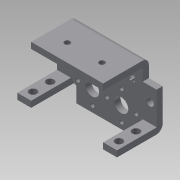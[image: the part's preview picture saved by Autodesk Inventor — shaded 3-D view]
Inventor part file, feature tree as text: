
AUTODESK INVENTOR PART (.ipt)
format: ipt  version: 2015 SP1 (Build 190203100, 203)  size: 531,456 bytes
history: native  units: mm
features: sketch x19, extrude x18, reference x11, projected_geometry x7, fillet x3, mirror x3
ambient origin geometry x8: Origin, YZ Plane, XZ Plane, XY Plane, X Axis, Y Axis, Z Axis, Center Point
bodies: Solid1 (feature_tree)
feature tree (61):
  extrude  "Extrusion1"  Depth=29.21mm
  extrude  "Extrusion2"  Depth=3.5mm
  extrude  "Extrusion3"  Depth=57.15mm TaperAngle=0.0deg
  sketch  "Sketch5"  dims[d8=57.15mm d9=0.0mm d11=25.147mm d12=0.0mm d13=0.254mm]
  extrude  "Extrusion4"  Depth=0.254mm TaperAngle=0.0deg
  fillet  "Fillet1"  Radius=0.254mm
  extrude  "Extrusion5"  Depth=3.75mm
  mirror  "Mirror1"
  fillet  "Fillet2"  Radius=22.4282mm
  extrude  "Extrusion6"  Depth=25.147mm TaperAngle=0.0deg
  extrude  "Extrusion7"  Depth=3.5mm TaperAngle=0.0deg
  extrude  "Extrusion8"  Depth=3.5mm TaperAngle=0.0deg
  extrude  "Extrusion9"  Depth=22.682mm TaperAngle=0.0deg
  extrude  "Extrusion10"  Depth=7.95mm TaperAngle=0.0deg
  sketch  "Sketch16"  dims[d38=7.95mm d39=0.0mm d43=7.95mm d44=0.0mm d47=3.5mm d48=0.0mm]
  extrude  "Extrusion11"  Depth=7.95mm TaperAngle=0.0deg
  fillet  "Fillet3"  Radius=3.5mm
  sketch  "Sketch19"  dims[d50=2.0mm d51=3.5mm d52=0.0mm]
  extrude  "Extrusion12"  Depth=3.5mm TaperAngle=0.0deg
  mirror  "Mirror2"
  extrude  "Extrusion13"  Depth=3.5mm TaperAngle=0.0deg
  extrude  "Extrusion15"  [1 undecoded]
  sketch  "Sketch24"
  sketch  "Sketch25"
  extrude  "Extrusion17"  [1 undecoded]
  extrude  "Extrusion18"  [1 undecoded]
  mirror  "Mirror4"
  extrude  "Extrusion19"  [1 undecoded]
  extrude  "Extrusion20"  [1 undecoded]
  sketch  "Sketch1"  dims[d0=57.15mm d1=29.21mm]
  sketch  "Sketch2"  dims[d2=3.5mm d3=0.0mm d4=3.5mm]
  sketch  "Sketch4"  dims[d5=3.5mm d6=57.15mm d7=0.0mm]
  sketch  "Sketch9"  dims[d15=25.147mm d16=0.0mm d17=3.75mm d18=22.4282mm]
  reference  "Reference3"
  reference  "Reference4"
  sketch  "Sketch11"  dims[d19=22.428mm d20=25.147mm d21=0.0mm]
  reference  "Reference7"
  sketch  "Sketch12"  dims[d22=25.147mm d23=0.0mm d24=3.5mm d25=0.0mm]
  reference  "Reference8"
  reference  "Reference9"
  sketch  "Sketch13"  dims[d26=3.5mm d27=0.0mm d28=3.5mm d29=0.0mm]
  sketch  "Sketch14"  dims[d30=3.5mm d33=22.682mm d34=0.0mm]
  sketch  "Sketch15"  dims[d35=0.254mm d36=7.95mm d37=0.0mm]
  reference  "Reference24"
  projected_geometry  "Projected Loop1"
  sketch  "Sketch21"  dims[d53=3.5mm d54=0.0mm d55=3.5mm d56=0.0mm]
  projected_geometry  "Projected Loop2"
  sketch  "Sketch23"
  reference  "Reference26"
  reference  "Reference27"
  reference  "Reference28"
  reference  "Reference29"
  reference  "Reference30"
  sketch  "Sketch26"
  sketch  "Sketch27"
  sketch  "Sketch28"
  projected_geometry  "Projected Loop3"
  projected_geometry  "Projected Loop4"
  projected_geometry  "Projected Loop5"
  projected_geometry  "Projected Loop6"
  projected_geometry  "Projected Loop7"
note: 5 required parameter values undecoded (feature->parameter linkage not recoverable at this tier; creation-order binding heuristic only, values carry confidence <= 0.55)
